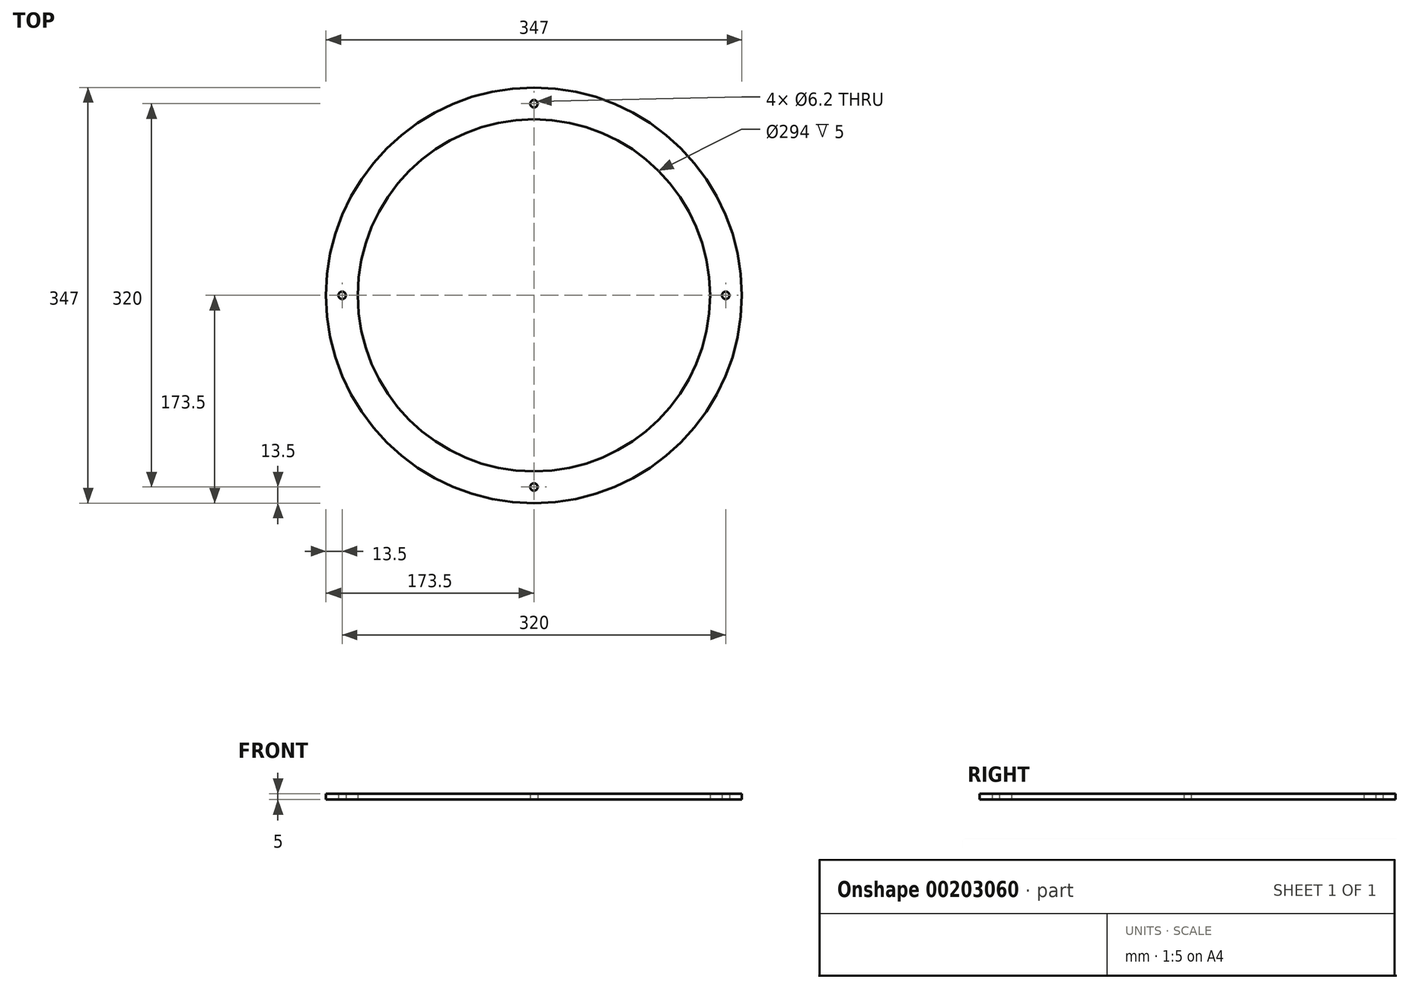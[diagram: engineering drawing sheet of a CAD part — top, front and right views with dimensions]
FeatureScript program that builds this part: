
annotation { "Feature Type Name" : "Feature", "Feature Type Description" : "" }
export const myFeature = defineFeature(function(context is Context, id is Id, definition is map)
    precondition{}
    {
        {
            var Q0;
            Q0=qCreatedBy(makeId("Top.planeOp"),FACE);
            var sketch = newSketch(context, id + "F0", { "sketchPlane" : qUnion([Q0])});
            skCircle(sketch, "E0", {"center": v(0, 0) * mm, "radius": 173.5 * mm});
            skCircle(sketch, "E1", {"center": v(0, 0) * mm, "radius": 147 * mm});
            skCircle(sketch, "E2", {"center": v(0, 160) * mm, "radius": 3.1 * mm});
            skCircle(sketch, "E3", {"center": v(160, 0) * mm, "radius": 3.1 * mm});
            skCircle(sketch, "E4", {"center": v(-160, 0) * mm, "radius": 3.1 * mm});
            skCircle(sketch, "E5", {"center": v(0, -160) * mm, "radius": 3.1 * mm});
            skSolve(sketch);
        }
        {
            var Q0;
            Q0=makeQuery(id+"F0.imprint","IMPRINT",FACE,{"disambiguationData":[TD([[makeQuery(id+"F0.imprint","IMPRINT",EDGE,{"derivedFrom":sQuery(id+"F0.wireOp",EDGE,"E0")}),1.0]])]});
            extrude(context, id + "F1", {"entities" : qUnion([Q0]), "depth" : 5 * mm});
        }
    });
